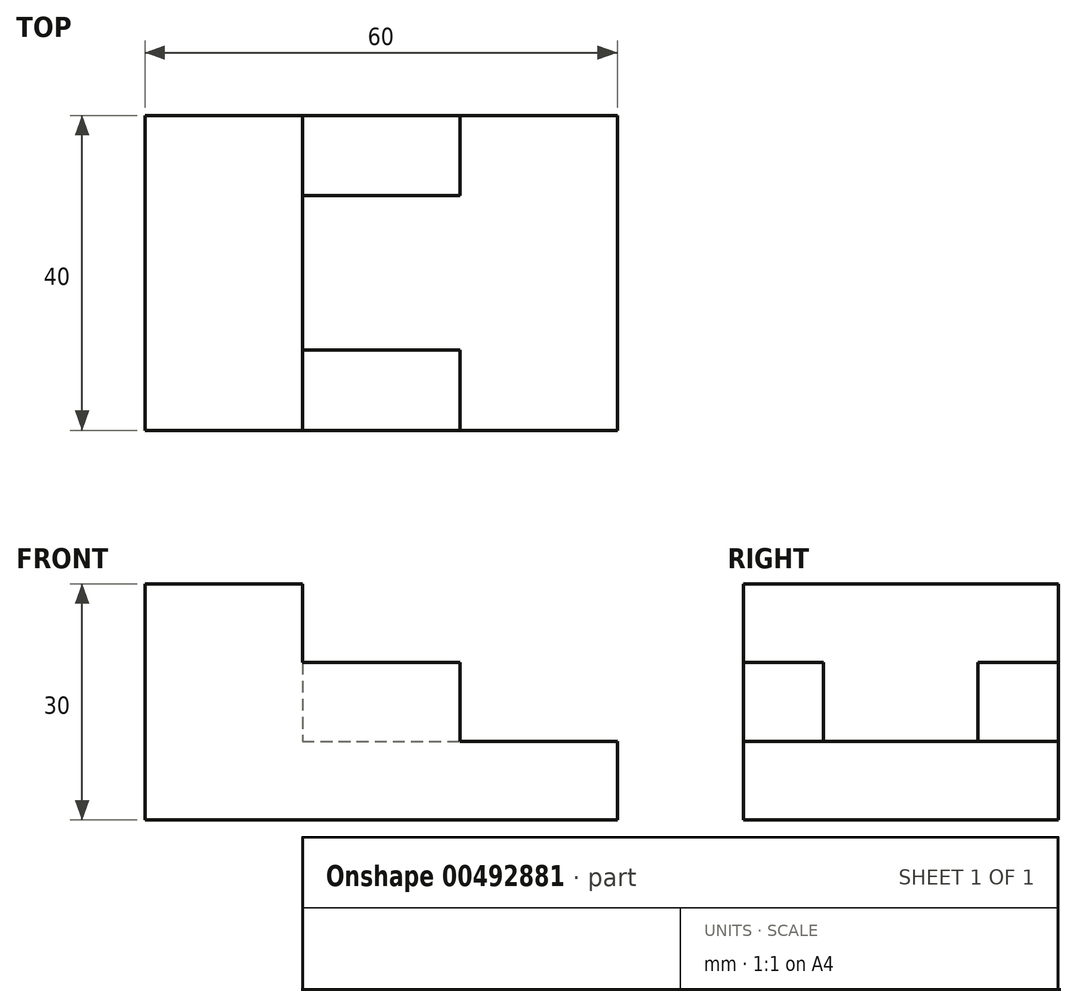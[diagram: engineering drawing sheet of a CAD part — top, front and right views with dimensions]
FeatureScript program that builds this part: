
annotation { "Feature Type Name" : "Feature", "Feature Type Description" : "" }
export const myFeature = defineFeature(function(context is Context, id is Id, definition is map)
    precondition{}
    {
        {
            var Q0;
            Q0=qCreatedBy(makeId("Top.planeOp"),FACE);
            var sketch = newSketch(context, id + "F0", { "sketchPlane" : qUnion([Q0])});
            skLineSegment(sketch, "E0", {"start": v(0, 0) * mm, "end": v(0, 40) * mm});
            skLineSegment(sketch, "E1", {"start": v(0, 40) * mm, "end": v(60, 40) * mm});
            skLineSegment(sketch, "E2", {"start": v(60, 40) * mm, "end": v(60, 0) * mm});
            skLineSegment(sketch, "E3", {"start": v(60, 0) * mm, "end": v(0, 0) * mm});
            skSolve(sketch);
        }
        {
            var Q0;
            Q0=makeQuery(id+"F0.imprint","IMPRINT",FACE,{"disambiguationData":[TD([[makeQuery(id+"F0.imprint","IMPRINT",EDGE,{"derivedFrom":sQuery(id+"F0.wireOp",EDGE,"E0")}),-1.0]])]});
            extrude(context, id + "F1", {"entities" : qUnion([Q0]), "depth" : 10 * mm});
        }
        {
            var Q0;
            Q0=makeQuery(id+"F1.opExtrude","CAP_FACE",FACE,{"disambiguationData":[OSD([sQuery(id+"F0.wireOp",EDGE,"E0"),sQuery(id+"F0.wireOp",EDGE,"E1"),sQuery(id+"F0.wireOp",EDGE,"E2"),sQuery(id+"F0.wireOp",EDGE,"E3")])],"isStart":false});
            var sketch = newSketch(context, id + "F2", { "sketchPlane" : qUnion([Q0])});
            skLineSegment(sketch, "E4", {"start": v(0, 40) * mm, "end": v(0, 0) * mm});
            skLineSegment(sketch, "E5", {"start": v(0, 0) * mm, "end": v(20, 0) * mm});
            skLineSegment(sketch, "E6", {"start": v(20, 0) * mm, "end": v(20, 40) * mm});
            skLineSegment(sketch, "E7", {"start": v(20, 40) * mm, "end": v(0, 40) * mm});
            skSolve(sketch);
        }
        {
            var Q0;
            Q0=makeQuery(id+"F2.imprint","IMPRINT",FACE,{"disambiguationData":[TD([[makeQuery(id+"F2.imprint","IMPRINT",EDGE,{"derivedFrom":sQuery(id+"F2.wireOp",EDGE,"E4")}),-1.0]])]});
            extrude(context, id + "F3", {"entities" : qUnion([Q0]), "operationType" : NewBodyOperationType.ADD, "depth" : 20 * mm});
        }
        {
            var Q0;
            Q0=makeQuery(id+"F1.opExtrude","CAP_FACE",FACE,{"disambiguationData":[OSD([sQuery(id+"F0.wireOp",EDGE,"E0"),sQuery(id+"F0.wireOp",EDGE,"E1"),sQuery(id+"F0.wireOp",EDGE,"E2"),sQuery(id+"F0.wireOp",EDGE,"E3")])],"isStart":false});
            var sketch = newSketch(context, id + "F4", { "sketchPlane" : qUnion([Q0])});
            skLineSegment(sketch, "E8", {"start": v(20, 29.8) * mm, "end": v(40, 29.8) * mm});
            skLineSegment(sketch, "E9", {"start": v(40, 29.8) * mm, "end": v(40, 40) * mm});
            skLineSegment(sketch, "E10", {"start": v(20, 20) * mm, "end": v(60, 20) * mm});
            skLineSegment(sketch, "E11.MirrorCS", {"start": v(20, 10.2) * mm, "end": v(40, 10.2) * mm});
            skLineSegment(sketch, "E12.MirrorCS", {"start": v(40, 10.2) * mm, "end": v(40, 0) * mm});
            skSolve(sketch);
        }
        {
            var Q0;
            {var subQ0=sQuery(id+"F4.wireOp",EDGE,"E8");Q0=makeQuery(id+"F4.imprint","IMPRINT",FACE,{"disambiguationData":[TD([[makeQuery(id+"F4.imprint","IMPRINT",EDGE,{"derivedFrom":subQ0}),1.0]])]});}
            var Q1;
            {var subQ0=sQuery(id+"F4.wireOp",EDGE,"E11.MirrorCS");Q1=makeQuery(id+"F4.imprint","IMPRINT",FACE,{"disambiguationData":[TD([[makeQuery(id+"F4.imprint","IMPRINT",EDGE,{"derivedFrom":subQ0}),-1.0]])]});}
            extrude(context, id + "F5", {"entities" : qUnion([Q0, Q1]), "operationType" : NewBodyOperationType.ADD, "depth" : 10 * mm});
        }
        {
            var Q0;
            {var subQ0=sQuery(id+"F4.wireOp",EDGE,"E8");Q0=makeQuery(id+"F4.imprint","IMPRINT",FACE,{"disambiguationData":[TD([[makeQuery(id+"F4.imprint","IMPRINT",EDGE,{"derivedFrom":subQ0}),1.0]])]});}
            extrude(context, id + "F6", {"entities" : qUnion([Q0]), "operationType" : NewBodyOperationType.ADD, "depth" : 10 * mm});
        }
    });
